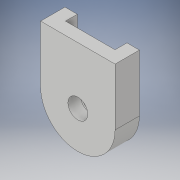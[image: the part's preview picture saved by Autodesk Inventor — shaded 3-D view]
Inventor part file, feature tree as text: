
AUTODESK INVENTOR PART (.ipt)
format: ipt  version: 2017 (Build 210142000, 142)  size: 132,608 bytes
history: native  units: in
note: dims shown in document units (in); Inventor stores cm internally (conversion verified against a paired STEP export)
features: extrude x4, sketch x4, projected_geometry x1
ambient origin geometry x8: Origin, YZ Plane, XZ Plane, XY Plane, X Axis, Y Axis, Z Axis, Center Point
bodies: Solid1 (feature_tree)
feature tree (9):
  extrude  "Extrusion1"  Depth=0.5in
  extrude  "Extrusion2"  Depth=0.125in TaperAngle=0.0deg
  extrude  "Extrusion3"  Depth=0.245in TaperAngle=0.0deg
  extrude  "Extrusion4"  Depth=0.12in
  sketch  "Sketch1"  dims[d0=0.5in d1=0.7in]
  sketch  "Sketch2"  dims[d2=0.25in d3=0.125in d4=0.0in]
  projected_geometry  "Projected Loop1"
  sketch  "Sketch3"  dims[d5=0.125in d6=0.245in d7=0.0in]
  sketch  "Sketch4"  dims[d8=0.12in d9=0.0in d10=0.2in d11=1.0in d12=0.0in]
